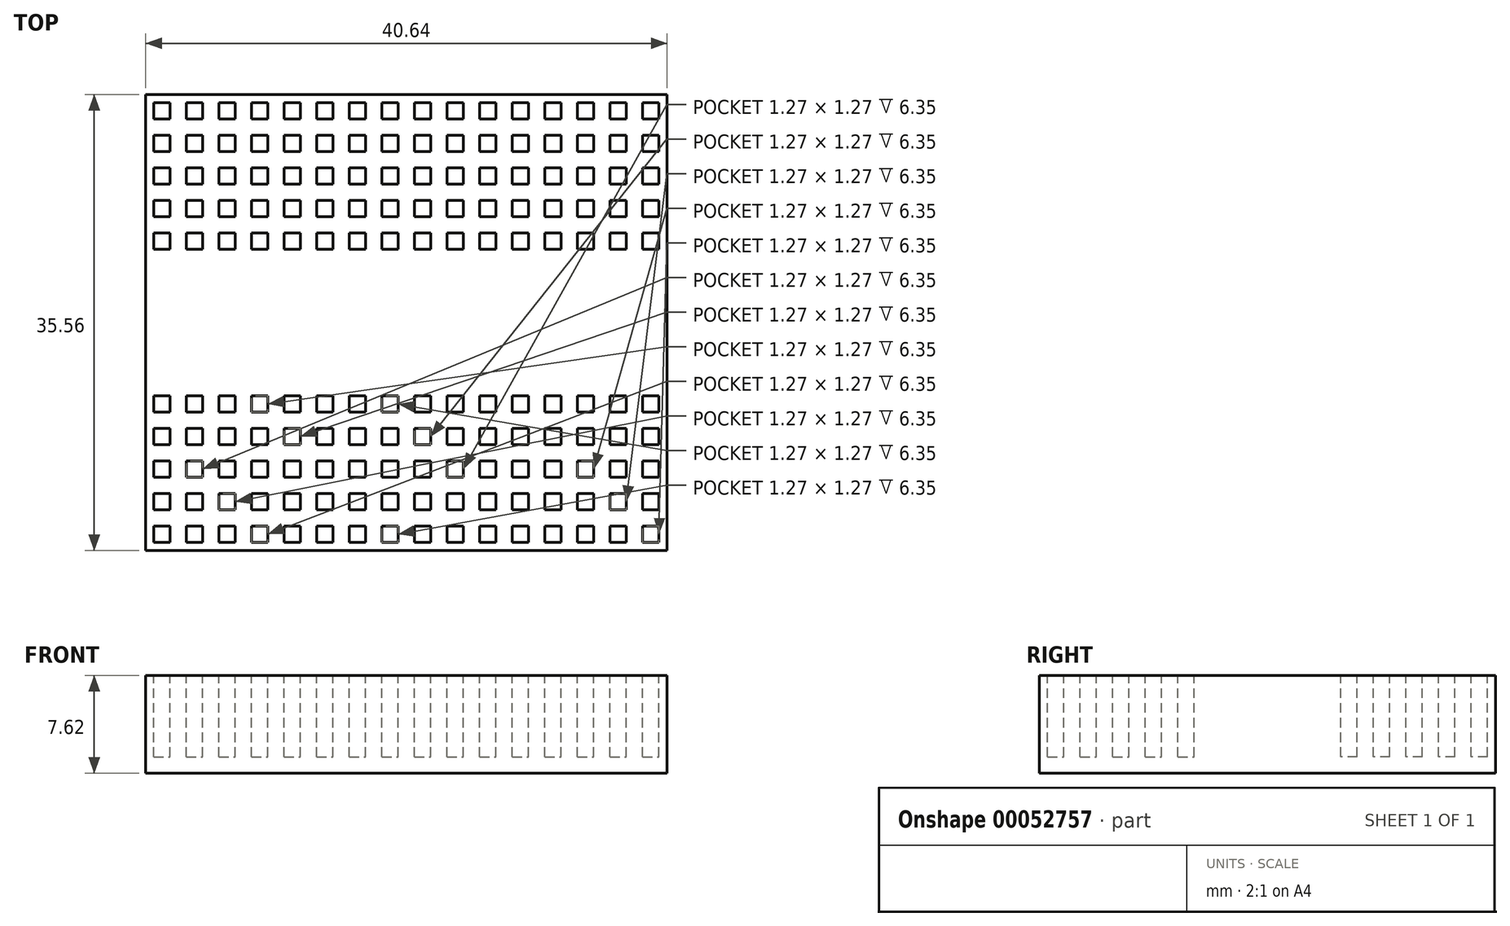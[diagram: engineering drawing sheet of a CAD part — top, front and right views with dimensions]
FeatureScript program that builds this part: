
annotation { "Feature Type Name" : "Feature", "Feature Type Description" : "" }
export const myFeature = defineFeature(function(context is Context, id is Id, definition is map)
    precondition{}
    {
        {
            var Q0;
            Q0=qCreatedBy(makeId("Top.planeOp"),FACE);
            var sketch = newSketch(context, id + "F0", { "sketchPlane" : qUnion([Q0])});
            skLineSegment(sketch, "E0.bottom", {"start": v(-20.32, 17.78) * mm, "end": v(20.32, 17.78) * mm});
            skLineSegment(sketch, "E0.top", {"start": v(-20.32, -17.78) * mm, "end": v(20.32, -17.78) * mm});
            skLineSegment(sketch, "E0.left", {"start": v(-20.32, 17.78) * mm, "end": v(-20.32, -17.78) * mm});
            skLineSegment(sketch, "E0.right", {"start": v(20.32, 17.78) * mm, "end": v(20.32, -17.78) * mm});
            skLineSegment(sketch, "E1", {"start": v(-20.32, 17.78) * mm, "end": v(20.32, -17.78) * mm, "construction": true});
            skSolve(sketch);
        }
        {
            var Q0;
            Q0 = qSketchRegion(id + "F0", true);
            extrude(context, id + "F1", {"entities" : qUnion([Q0]), "depth" : 7.62 * mm});
        }
        {
            var Q0;
            Q0=makeQuery(id+"F1.opExtrude","CAP_FACE",FACE,{"disambiguationData":[OSD([sQuery(id+"F0.wireOp",EDGE,"E0.bottom"),sQuery(id+"F0.wireOp",EDGE,"E0.top"),sQuery(id+"F0.wireOp",EDGE,"E0.left"),sQuery(id+"F0.wireOp",EDGE,"E0.right")])],"isStart":false});
            var sketch = newSketch(context, id + "F2", { "sketchPlane" : qUnion([Q0])});
            skLineSegment(sketch, "E2.bottom", {"start": v(-19.69, 17.15) * mm, "end": v(-18.42, 17.15) * mm});
            skLineSegment(sketch, "E2.top", {"start": v(-19.69, 15.88) * mm, "end": v(-18.42, 15.88) * mm});
            skLineSegment(sketch, "E2.left", {"start": v(-19.69, 17.15) * mm, "end": v(-19.69, 15.88) * mm});
            skLineSegment(sketch, "E2.right", {"start": v(-18.42, 17.15) * mm, "end": v(-18.42, 15.88) * mm});
            skLineSegment(sketch, "E3.0.1.0", {"start": v(-19.69, 14.6) * mm, "end": v(-18.42, 14.6) * mm});
            skLineSegment(sketch, "E3.0.1.1", {"start": v(-19.69, 14.6) * mm, "end": v(-19.69, 13.34) * mm});
            skLineSegment(sketch, "E3.0.1.2", {"start": v(-18.42, 14.6) * mm, "end": v(-18.42, 13.34) * mm});
            skLineSegment(sketch, "E3.0.1.3", {"start": v(-19.69, 13.34) * mm, "end": v(-18.42, 13.34) * mm});
            skLineSegment(sketch, "E3.0.2.0", {"start": v(-19.69, 12.07) * mm, "end": v(-18.42, 12.07) * mm});
            skLineSegment(sketch, "E3.0.2.1", {"start": v(-19.69, 12.07) * mm, "end": v(-19.69, 10.8) * mm});
            skLineSegment(sketch, "E3.0.2.2", {"start": v(-18.42, 12.07) * mm, "end": v(-18.42, 10.8) * mm});
            skLineSegment(sketch, "E3.0.2.3", {"start": v(-19.69, 10.8) * mm, "end": v(-18.42, 10.8) * mm});
            skLineSegment(sketch, "E3.0.3.0", {"start": v(-19.69, 9.53) * mm, "end": v(-18.42, 9.53) * mm});
            skLineSegment(sketch, "E3.0.3.1", {"start": v(-19.69, 9.53) * mm, "end": v(-19.69, 8.26) * mm});
            skLineSegment(sketch, "E3.0.3.2", {"start": v(-18.42, 9.53) * mm, "end": v(-18.42, 8.26) * mm});
            skLineSegment(sketch, "E3.0.3.3", {"start": v(-19.69, 8.26) * mm, "end": v(-18.42, 8.26) * mm});
            skLineSegment(sketch, "E3.0.4.0", {"start": v(-19.69, 6.99) * mm, "end": v(-18.42, 6.99) * mm});
            skLineSegment(sketch, "E3.0.4.1", {"start": v(-19.69, 6.99) * mm, "end": v(-19.69, 5.72) * mm});
            skLineSegment(sketch, "E3.0.4.2", {"start": v(-18.42, 6.99) * mm, "end": v(-18.42, 5.72) * mm});
            skLineSegment(sketch, "E3.0.4.3", {"start": v(-19.69, 5.72) * mm, "end": v(-18.42, 5.72) * mm});
            skLineSegment(sketch, "E3.1.0.0", {"start": v(-17.15, 17.15) * mm, "end": v(-15.88, 17.15) * mm});
            skLineSegment(sketch, "E3.1.0.1", {"start": v(-17.15, 17.15) * mm, "end": v(-17.15, 15.88) * mm});
            skLineSegment(sketch, "E3.1.0.2", {"start": v(-15.88, 17.15) * mm, "end": v(-15.88, 15.88) * mm});
            skLineSegment(sketch, "E3.1.0.3", {"start": v(-17.15, 15.88) * mm, "end": v(-15.88, 15.88) * mm});
            skLineSegment(sketch, "E3.1.1.0", {"start": v(-17.15, 14.6) * mm, "end": v(-15.88, 14.6) * mm});
            skLineSegment(sketch, "E3.1.1.1", {"start": v(-17.15, 14.6) * mm, "end": v(-17.15, 13.34) * mm});
            skLineSegment(sketch, "E3.1.1.2", {"start": v(-15.88, 14.6) * mm, "end": v(-15.88, 13.34) * mm});
            skLineSegment(sketch, "E3.1.1.3", {"start": v(-17.15, 13.34) * mm, "end": v(-15.88, 13.34) * mm});
            skLineSegment(sketch, "E3.1.2.0", {"start": v(-17.15, 12.07) * mm, "end": v(-15.88, 12.07) * mm});
            skLineSegment(sketch, "E3.1.2.1", {"start": v(-17.15, 12.07) * mm, "end": v(-17.15, 10.8) * mm});
            skLineSegment(sketch, "E3.1.2.2", {"start": v(-15.88, 12.07) * mm, "end": v(-15.88, 10.8) * mm});
            skLineSegment(sketch, "E3.1.2.3", {"start": v(-17.15, 10.8) * mm, "end": v(-15.88, 10.8) * mm});
            skLineSegment(sketch, "E3.1.3.0", {"start": v(-17.15, 9.53) * mm, "end": v(-15.88, 9.53) * mm});
            skLineSegment(sketch, "E3.1.3.1", {"start": v(-17.15, 9.53) * mm, "end": v(-17.15, 8.26) * mm});
            skLineSegment(sketch, "E3.1.3.2", {"start": v(-15.88, 9.53) * mm, "end": v(-15.88, 8.26) * mm});
            skLineSegment(sketch, "E3.1.3.3", {"start": v(-17.15, 8.26) * mm, "end": v(-15.88, 8.26) * mm});
            skLineSegment(sketch, "E3.1.4.0", {"start": v(-17.15, 6.99) * mm, "end": v(-15.88, 6.99) * mm});
            skLineSegment(sketch, "E3.1.4.1", {"start": v(-17.15, 6.99) * mm, "end": v(-17.15, 5.72) * mm});
            skLineSegment(sketch, "E3.1.4.2", {"start": v(-15.88, 6.99) * mm, "end": v(-15.88, 5.72) * mm});
            skLineSegment(sketch, "E3.1.4.3", {"start": v(-17.15, 5.72) * mm, "end": v(-15.88, 5.72) * mm});
            skLineSegment(sketch, "E3.2.0.0", {"start": v(-14.6, 17.15) * mm, "end": v(-13.34, 17.15) * mm});
            skLineSegment(sketch, "E3.2.0.1", {"start": v(-14.6, 17.15) * mm, "end": v(-14.6, 15.88) * mm});
            skLineSegment(sketch, "E3.2.0.2", {"start": v(-13.34, 17.15) * mm, "end": v(-13.34, 15.88) * mm});
            skLineSegment(sketch, "E3.2.0.3", {"start": v(-14.6, 15.88) * mm, "end": v(-13.34, 15.88) * mm});
            skLineSegment(sketch, "E3.2.1.0", {"start": v(-14.6, 14.6) * mm, "end": v(-13.34, 14.6) * mm});
            skLineSegment(sketch, "E3.2.1.1", {"start": v(-14.6, 14.6) * mm, "end": v(-14.6, 13.34) * mm});
            skLineSegment(sketch, "E3.2.1.2", {"start": v(-13.34, 14.6) * mm, "end": v(-13.34, 13.34) * mm});
            skLineSegment(sketch, "E3.2.1.3", {"start": v(-14.6, 13.34) * mm, "end": v(-13.34, 13.34) * mm});
            skLineSegment(sketch, "E3.2.2.0", {"start": v(-14.6, 12.07) * mm, "end": v(-13.34, 12.07) * mm});
            skLineSegment(sketch, "E3.2.2.1", {"start": v(-14.6, 12.07) * mm, "end": v(-14.6, 10.8) * mm});
            skLineSegment(sketch, "E3.2.2.2", {"start": v(-13.34, 12.07) * mm, "end": v(-13.34, 10.8) * mm});
            skLineSegment(sketch, "E3.2.2.3", {"start": v(-14.6, 10.8) * mm, "end": v(-13.34, 10.8) * mm});
            skLineSegment(sketch, "E3.2.3.0", {"start": v(-14.6, 9.53) * mm, "end": v(-13.34, 9.53) * mm});
            skLineSegment(sketch, "E3.2.3.1", {"start": v(-14.6, 9.53) * mm, "end": v(-14.6, 8.26) * mm});
            skLineSegment(sketch, "E3.2.3.2", {"start": v(-13.34, 9.53) * mm, "end": v(-13.34, 8.26) * mm});
            skLineSegment(sketch, "E3.2.3.3", {"start": v(-14.6, 8.26) * mm, "end": v(-13.34, 8.26) * mm});
            skLineSegment(sketch, "E3.2.4.0", {"start": v(-14.6, 6.99) * mm, "end": v(-13.34, 6.99) * mm});
            skLineSegment(sketch, "E3.2.4.1", {"start": v(-14.6, 6.99) * mm, "end": v(-14.6, 5.72) * mm});
            skLineSegment(sketch, "E3.2.4.2", {"start": v(-13.34, 6.99) * mm, "end": v(-13.34, 5.72) * mm});
            skLineSegment(sketch, "E3.2.4.3", {"start": v(-14.6, 5.72) * mm, "end": v(-13.34, 5.72) * mm});
            skLineSegment(sketch, "E3.3.0.0", {"start": v(-12.07, 17.15) * mm, "end": v(-10.8, 17.15) * mm});
            skLineSegment(sketch, "E3.3.0.1", {"start": v(-12.07, 17.15) * mm, "end": v(-12.07, 15.88) * mm});
            skLineSegment(sketch, "E3.3.0.2", {"start": v(-10.8, 17.15) * mm, "end": v(-10.8, 15.88) * mm});
            skLineSegment(sketch, "E3.3.0.3", {"start": v(-12.07, 15.88) * mm, "end": v(-10.8, 15.88) * mm});
            skLineSegment(sketch, "E3.3.1.0", {"start": v(-12.07, 14.6) * mm, "end": v(-10.8, 14.6) * mm});
            skLineSegment(sketch, "E3.3.1.1", {"start": v(-12.07, 14.6) * mm, "end": v(-12.07, 13.34) * mm});
            skLineSegment(sketch, "E3.3.1.2", {"start": v(-10.8, 14.6) * mm, "end": v(-10.8, 13.34) * mm});
            skLineSegment(sketch, "E3.3.1.3", {"start": v(-12.07, 13.34) * mm, "end": v(-10.8, 13.34) * mm});
            skLineSegment(sketch, "E3.3.2.0", {"start": v(-12.07, 12.07) * mm, "end": v(-10.8, 12.07) * mm});
            skLineSegment(sketch, "E3.3.2.1", {"start": v(-12.07, 12.07) * mm, "end": v(-12.07, 10.8) * mm});
            skLineSegment(sketch, "E3.3.2.2", {"start": v(-10.8, 12.07) * mm, "end": v(-10.8, 10.8) * mm});
            skLineSegment(sketch, "E3.3.2.3", {"start": v(-12.07, 10.8) * mm, "end": v(-10.8, 10.8) * mm});
            skLineSegment(sketch, "E3.3.3.0", {"start": v(-12.07, 9.53) * mm, "end": v(-10.8, 9.53) * mm});
            skLineSegment(sketch, "E3.3.3.1", {"start": v(-12.07, 9.53) * mm, "end": v(-12.07, 8.26) * mm});
            skLineSegment(sketch, "E3.3.3.2", {"start": v(-10.8, 9.53) * mm, "end": v(-10.8, 8.26) * mm});
            skLineSegment(sketch, "E3.3.3.3", {"start": v(-12.07, 8.26) * mm, "end": v(-10.8, 8.26) * mm});
            skLineSegment(sketch, "E3.3.4.0", {"start": v(-12.07, 6.99) * mm, "end": v(-10.8, 6.99) * mm});
            skLineSegment(sketch, "E3.3.4.1", {"start": v(-12.07, 6.99) * mm, "end": v(-12.07, 5.72) * mm});
            skLineSegment(sketch, "E3.3.4.2", {"start": v(-10.8, 6.99) * mm, "end": v(-10.8, 5.72) * mm});
            skLineSegment(sketch, "E3.3.4.3", {"start": v(-12.07, 5.72) * mm, "end": v(-10.8, 5.72) * mm});
            skLineSegment(sketch, "E3.4.0.0", {"start": v(-9.53, 17.15) * mm, "end": v(-8.26, 17.15) * mm});
            skLineSegment(sketch, "E3.4.0.1", {"start": v(-9.53, 17.15) * mm, "end": v(-9.53, 15.88) * mm});
            skLineSegment(sketch, "E3.4.0.2", {"start": v(-8.26, 17.15) * mm, "end": v(-8.26, 15.88) * mm});
            skLineSegment(sketch, "E3.4.0.3", {"start": v(-9.53, 15.88) * mm, "end": v(-8.26, 15.88) * mm});
            skLineSegment(sketch, "E3.4.1.0", {"start": v(-9.53, 14.6) * mm, "end": v(-8.26, 14.6) * mm});
            skLineSegment(sketch, "E3.4.1.1", {"start": v(-9.53, 14.6) * mm, "end": v(-9.53, 13.34) * mm});
            skLineSegment(sketch, "E3.4.1.2", {"start": v(-8.26, 14.6) * mm, "end": v(-8.26, 13.34) * mm});
            skLineSegment(sketch, "E3.4.1.3", {"start": v(-9.53, 13.34) * mm, "end": v(-8.26, 13.34) * mm});
            skLineSegment(sketch, "E3.4.2.0", {"start": v(-9.53, 12.07) * mm, "end": v(-8.26, 12.07) * mm});
            skLineSegment(sketch, "E3.4.2.1", {"start": v(-9.53, 12.07) * mm, "end": v(-9.53, 10.8) * mm});
            skLineSegment(sketch, "E3.4.2.2", {"start": v(-8.26, 12.07) * mm, "end": v(-8.26, 10.8) * mm});
            skLineSegment(sketch, "E3.4.2.3", {"start": v(-9.53, 10.8) * mm, "end": v(-8.26, 10.8) * mm});
            skLineSegment(sketch, "E3.4.3.0", {"start": v(-9.53, 9.53) * mm, "end": v(-8.26, 9.53) * mm});
            skLineSegment(sketch, "E3.4.3.1", {"start": v(-9.53, 9.53) * mm, "end": v(-9.53, 8.26) * mm});
            skLineSegment(sketch, "E3.4.3.2", {"start": v(-8.26, 9.53) * mm, "end": v(-8.26, 8.26) * mm});
            skLineSegment(sketch, "E3.4.3.3", {"start": v(-9.53, 8.26) * mm, "end": v(-8.26, 8.26) * mm});
            skLineSegment(sketch, "E3.4.4.0", {"start": v(-9.53, 6.99) * mm, "end": v(-8.26, 6.99) * mm});
            skLineSegment(sketch, "E3.4.4.1", {"start": v(-9.53, 6.99) * mm, "end": v(-9.53, 5.72) * mm});
            skLineSegment(sketch, "E3.4.4.2", {"start": v(-8.26, 6.99) * mm, "end": v(-8.26, 5.72) * mm});
            skLineSegment(sketch, "E3.4.4.3", {"start": v(-9.53, 5.72) * mm, "end": v(-8.26, 5.72) * mm});
            skLineSegment(sketch, "E3.5.0.0", {"start": v(-6.99, 17.15) * mm, "end": v(-5.72, 17.15) * mm});
            skLineSegment(sketch, "E3.5.0.1", {"start": v(-6.99, 17.15) * mm, "end": v(-6.99, 15.88) * mm});
            skLineSegment(sketch, "E3.5.0.2", {"start": v(-5.72, 17.15) * mm, "end": v(-5.72, 15.88) * mm});
            skLineSegment(sketch, "E3.5.0.3", {"start": v(-6.99, 15.88) * mm, "end": v(-5.72, 15.88) * mm});
            skLineSegment(sketch, "E3.5.1.0", {"start": v(-6.99, 14.6) * mm, "end": v(-5.72, 14.6) * mm});
            skLineSegment(sketch, "E3.5.1.1", {"start": v(-6.99, 14.6) * mm, "end": v(-6.99, 13.34) * mm});
            skLineSegment(sketch, "E3.5.1.2", {"start": v(-5.72, 14.6) * mm, "end": v(-5.72, 13.34) * mm});
            skLineSegment(sketch, "E3.5.1.3", {"start": v(-6.99, 13.34) * mm, "end": v(-5.72, 13.34) * mm});
            skLineSegment(sketch, "E3.5.2.0", {"start": v(-6.99, 12.07) * mm, "end": v(-5.72, 12.07) * mm});
            skLineSegment(sketch, "E3.5.2.1", {"start": v(-6.99, 12.07) * mm, "end": v(-6.99, 10.8) * mm});
            skLineSegment(sketch, "E3.5.2.2", {"start": v(-5.72, 12.07) * mm, "end": v(-5.72, 10.8) * mm});
            skLineSegment(sketch, "E3.5.2.3", {"start": v(-6.99, 10.8) * mm, "end": v(-5.72, 10.8) * mm});
            skLineSegment(sketch, "E3.5.3.0", {"start": v(-6.99, 9.53) * mm, "end": v(-5.72, 9.53) * mm});
            skLineSegment(sketch, "E3.5.3.1", {"start": v(-6.99, 9.53) * mm, "end": v(-6.99, 8.26) * mm});
            skLineSegment(sketch, "E3.5.3.2", {"start": v(-5.72, 9.53) * mm, "end": v(-5.72, 8.26) * mm});
            skLineSegment(sketch, "E3.5.3.3", {"start": v(-6.99, 8.26) * mm, "end": v(-5.72, 8.26) * mm});
            skLineSegment(sketch, "E3.5.4.0", {"start": v(-6.99, 6.99) * mm, "end": v(-5.72, 6.99) * mm});
            skLineSegment(sketch, "E3.5.4.1", {"start": v(-6.99, 6.99) * mm, "end": v(-6.99, 5.72) * mm});
            skLineSegment(sketch, "E3.5.4.2", {"start": v(-5.72, 6.99) * mm, "end": v(-5.72, 5.72) * mm});
            skLineSegment(sketch, "E3.5.4.3", {"start": v(-6.99, 5.72) * mm, "end": v(-5.72, 5.72) * mm});
            skLineSegment(sketch, "E3.6.0.0", {"start": v(-4.45, 17.15) * mm, "end": v(-3.18, 17.15) * mm});
            skLineSegment(sketch, "E3.6.0.1", {"start": v(-4.45, 17.15) * mm, "end": v(-4.45, 15.88) * mm});
            skLineSegment(sketch, "E3.6.0.2", {"start": v(-3.18, 17.15) * mm, "end": v(-3.18, 15.88) * mm});
            skLineSegment(sketch, "E3.6.0.3", {"start": v(-4.45, 15.88) * mm, "end": v(-3.18, 15.88) * mm});
            skLineSegment(sketch, "E3.6.1.0", {"start": v(-4.45, 14.6) * mm, "end": v(-3.18, 14.6) * mm});
            skLineSegment(sketch, "E3.6.1.1", {"start": v(-4.45, 14.6) * mm, "end": v(-4.45, 13.34) * mm});
            skLineSegment(sketch, "E3.6.1.2", {"start": v(-3.18, 14.6) * mm, "end": v(-3.18, 13.34) * mm});
            skLineSegment(sketch, "E3.6.1.3", {"start": v(-4.45, 13.34) * mm, "end": v(-3.18, 13.34) * mm});
            skLineSegment(sketch, "E3.6.2.0", {"start": v(-4.45, 12.07) * mm, "end": v(-3.18, 12.07) * mm});
            skLineSegment(sketch, "E3.6.2.1", {"start": v(-4.45, 12.07) * mm, "end": v(-4.45, 10.8) * mm});
            skLineSegment(sketch, "E3.6.2.2", {"start": v(-3.18, 12.07) * mm, "end": v(-3.18, 10.8) * mm});
            skLineSegment(sketch, "E3.6.2.3", {"start": v(-4.45, 10.8) * mm, "end": v(-3.18, 10.8) * mm});
            skLineSegment(sketch, "E3.6.3.0", {"start": v(-4.45, 9.53) * mm, "end": v(-3.18, 9.53) * mm});
            skLineSegment(sketch, "E3.6.3.1", {"start": v(-4.45, 9.53) * mm, "end": v(-4.45, 8.26) * mm});
            skLineSegment(sketch, "E3.6.3.2", {"start": v(-3.18, 9.53) * mm, "end": v(-3.18, 8.26) * mm});
            skLineSegment(sketch, "E3.6.3.3", {"start": v(-4.45, 8.26) * mm, "end": v(-3.18, 8.26) * mm});
            skLineSegment(sketch, "E3.6.4.0", {"start": v(-4.45, 6.99) * mm, "end": v(-3.18, 6.99) * mm});
            skLineSegment(sketch, "E3.6.4.1", {"start": v(-4.45, 6.99) * mm, "end": v(-4.45, 5.72) * mm});
            skLineSegment(sketch, "E3.6.4.2", {"start": v(-3.18, 6.99) * mm, "end": v(-3.18, 5.72) * mm});
            skLineSegment(sketch, "E3.6.4.3", {"start": v(-4.45, 5.72) * mm, "end": v(-3.18, 5.72) * mm});
            skLineSegment(sketch, "E3.7.0.0", {"start": v(-1.9, 17.15) * mm, "end": v(-0.64, 17.15) * mm});
            skLineSegment(sketch, "E3.7.0.1", {"start": v(-1.9, 17.15) * mm, "end": v(-1.9, 15.88) * mm});
            skLineSegment(sketch, "E3.7.0.2", {"start": v(-0.63, 17.15) * mm, "end": v(-0.64, 15.88) * mm});
            skLineSegment(sketch, "E3.7.0.3", {"start": v(-1.9, 15.88) * mm, "end": v(-0.64, 15.88) * mm});
            skLineSegment(sketch, "E3.7.1.0", {"start": v(-1.9, 14.6) * mm, "end": v(-0.64, 14.6) * mm});
            skLineSegment(sketch, "E3.7.1.1", {"start": v(-1.9, 14.6) * mm, "end": v(-1.9, 13.34) * mm});
            skLineSegment(sketch, "E3.7.1.2", {"start": v(-0.63, 14.6) * mm, "end": v(-0.64, 13.34) * mm});
            skLineSegment(sketch, "E3.7.1.3", {"start": v(-1.9, 13.34) * mm, "end": v(-0.64, 13.34) * mm});
            skLineSegment(sketch, "E3.7.2.0", {"start": v(-1.9, 12.07) * mm, "end": v(-0.64, 12.07) * mm});
            skLineSegment(sketch, "E3.7.2.1", {"start": v(-1.9, 12.07) * mm, "end": v(-1.9, 10.8) * mm});
            skLineSegment(sketch, "E3.7.2.2", {"start": v(-0.63, 12.07) * mm, "end": v(-0.64, 10.8) * mm});
            skLineSegment(sketch, "E3.7.2.3", {"start": v(-1.9, 10.8) * mm, "end": v(-0.64, 10.8) * mm});
            skLineSegment(sketch, "E3.7.3.0", {"start": v(-1.9, 9.53) * mm, "end": v(-0.64, 9.53) * mm});
            skLineSegment(sketch, "E3.7.3.1", {"start": v(-1.9, 9.53) * mm, "end": v(-1.9, 8.26) * mm});
            skLineSegment(sketch, "E3.7.3.2", {"start": v(-0.63, 9.53) * mm, "end": v(-0.64, 8.26) * mm});
            skLineSegment(sketch, "E3.7.3.3", {"start": v(-1.9, 8.26) * mm, "end": v(-0.64, 8.26) * mm});
            skLineSegment(sketch, "E3.7.4.0", {"start": v(-1.9, 6.99) * mm, "end": v(-0.64, 6.99) * mm});
            skLineSegment(sketch, "E3.7.4.1", {"start": v(-1.9, 6.99) * mm, "end": v(-1.9, 5.72) * mm});
            skLineSegment(sketch, "E3.7.4.2", {"start": v(-0.63, 6.99) * mm, "end": v(-0.64, 5.72) * mm});
            skLineSegment(sketch, "E3.7.4.3", {"start": v(-1.9, 5.72) * mm, "end": v(-0.64, 5.72) * mm});
            skLineSegment(sketch, "E3.8.0.0", {"start": v(0.64, 17.15) * mm, "end": v(1.9, 17.15) * mm});
            skLineSegment(sketch, "E3.8.0.1", {"start": v(0.64, 17.15) * mm, "end": v(0.64, 15.88) * mm});
            skLineSegment(sketch, "E3.8.0.2", {"start": v(1.9, 17.15) * mm, "end": v(1.9, 15.88) * mm});
            skLineSegment(sketch, "E3.8.0.3", {"start": v(0.64, 15.88) * mm, "end": v(1.9, 15.88) * mm});
            skLineSegment(sketch, "E3.8.1.0", {"start": v(0.64, 14.6) * mm, "end": v(1.9, 14.6) * mm});
            skLineSegment(sketch, "E3.8.1.1", {"start": v(0.64, 14.6) * mm, "end": v(0.64, 13.34) * mm});
            skLineSegment(sketch, "E3.8.1.2", {"start": v(1.9, 14.6) * mm, "end": v(1.9, 13.34) * mm});
            skLineSegment(sketch, "E3.8.1.3", {"start": v(0.64, 13.34) * mm, "end": v(1.9, 13.34) * mm});
            skLineSegment(sketch, "E3.8.2.0", {"start": v(0.64, 12.07) * mm, "end": v(1.9, 12.07) * mm});
            skLineSegment(sketch, "E3.8.2.1", {"start": v(0.64, 12.07) * mm, "end": v(0.64, 10.8) * mm});
            skLineSegment(sketch, "E3.8.2.2", {"start": v(1.9, 12.07) * mm, "end": v(1.9, 10.8) * mm});
            skLineSegment(sketch, "E3.8.2.3", {"start": v(0.64, 10.8) * mm, "end": v(1.9, 10.8) * mm});
            skLineSegment(sketch, "E3.8.3.0", {"start": v(0.64, 9.53) * mm, "end": v(1.9, 9.53) * mm});
            skLineSegment(sketch, "E3.8.3.1", {"start": v(0.64, 9.53) * mm, "end": v(0.64, 8.26) * mm});
            skLineSegment(sketch, "E3.8.3.2", {"start": v(1.9, 9.53) * mm, "end": v(1.9, 8.26) * mm});
            skLineSegment(sketch, "E3.8.3.3", {"start": v(0.64, 8.26) * mm, "end": v(1.9, 8.26) * mm});
            skLineSegment(sketch, "E3.8.4.0", {"start": v(0.64, 6.99) * mm, "end": v(1.9, 6.99) * mm});
            skLineSegment(sketch, "E3.8.4.1", {"start": v(0.64, 6.99) * mm, "end": v(0.64, 5.72) * mm});
            skLineSegment(sketch, "E3.8.4.2", {"start": v(1.9, 6.99) * mm, "end": v(1.9, 5.72) * mm});
            skLineSegment(sketch, "E3.8.4.3", {"start": v(0.64, 5.72) * mm, "end": v(1.9, 5.72) * mm});
            skLineSegment(sketch, "E3.9.0.0", {"start": v(3.18, 17.15) * mm, "end": v(4.45, 17.15) * mm});
            skLineSegment(sketch, "E3.9.0.1", {"start": v(3.18, 17.15) * mm, "end": v(3.18, 15.88) * mm});
            skLineSegment(sketch, "E3.9.0.2", {"start": v(4.45, 17.15) * mm, "end": v(4.45, 15.88) * mm});
            skLineSegment(sketch, "E3.9.0.3", {"start": v(3.18, 15.88) * mm, "end": v(4.45, 15.88) * mm});
            skLineSegment(sketch, "E3.9.1.0", {"start": v(3.18, 14.6) * mm, "end": v(4.45, 14.6) * mm});
            skLineSegment(sketch, "E3.9.1.1", {"start": v(3.18, 14.6) * mm, "end": v(3.18, 13.34) * mm});
            skLineSegment(sketch, "E3.9.1.2", {"start": v(4.45, 14.6) * mm, "end": v(4.45, 13.34) * mm});
            skLineSegment(sketch, "E3.9.1.3", {"start": v(3.18, 13.34) * mm, "end": v(4.45, 13.34) * mm});
            skLineSegment(sketch, "E3.9.2.0", {"start": v(3.18, 12.07) * mm, "end": v(4.45, 12.07) * mm});
            skLineSegment(sketch, "E3.9.2.1", {"start": v(3.18, 12.07) * mm, "end": v(3.18, 10.8) * mm});
            skLineSegment(sketch, "E3.9.2.2", {"start": v(4.45, 12.07) * mm, "end": v(4.45, 10.8) * mm});
            skLineSegment(sketch, "E3.9.2.3", {"start": v(3.18, 10.8) * mm, "end": v(4.45, 10.8) * mm});
            skLineSegment(sketch, "E3.9.3.0", {"start": v(3.18, 9.53) * mm, "end": v(4.45, 9.53) * mm});
            skLineSegment(sketch, "E3.9.3.1", {"start": v(3.18, 9.53) * mm, "end": v(3.18, 8.26) * mm});
            skLineSegment(sketch, "E3.9.3.2", {"start": v(4.45, 9.53) * mm, "end": v(4.45, 8.26) * mm});
            skLineSegment(sketch, "E3.9.3.3", {"start": v(3.18, 8.26) * mm, "end": v(4.45, 8.26) * mm});
            skLineSegment(sketch, "E3.9.4.0", {"start": v(3.18, 6.99) * mm, "end": v(4.45, 6.99) * mm});
            skLineSegment(sketch, "E3.9.4.1", {"start": v(3.18, 6.99) * mm, "end": v(3.18, 5.72) * mm});
            skLineSegment(sketch, "E3.9.4.2", {"start": v(4.45, 6.99) * mm, "end": v(4.45, 5.72) * mm});
            skLineSegment(sketch, "E3.9.4.3", {"start": v(3.18, 5.72) * mm, "end": v(4.45, 5.72) * mm});
            skLineSegment(sketch, "E3.10.0.0", {"start": v(5.72, 17.15) * mm, "end": v(6.99, 17.15) * mm});
            skLineSegment(sketch, "E3.10.0.1", {"start": v(5.72, 17.15) * mm, "end": v(5.72, 15.88) * mm});
            skLineSegment(sketch, "E3.10.0.2", {"start": v(6.99, 17.15) * mm, "end": v(6.99, 15.88) * mm});
            skLineSegment(sketch, "E3.10.0.3", {"start": v(5.72, 15.88) * mm, "end": v(6.99, 15.88) * mm});
            skLineSegment(sketch, "E3.10.1.0", {"start": v(5.72, 14.6) * mm, "end": v(6.99, 14.6) * mm});
            skLineSegment(sketch, "E3.10.1.1", {"start": v(5.72, 14.6) * mm, "end": v(5.72, 13.34) * mm});
            skLineSegment(sketch, "E3.10.1.2", {"start": v(6.99, 14.6) * mm, "end": v(6.99, 13.34) * mm});
            skLineSegment(sketch, "E3.10.1.3", {"start": v(5.72, 13.34) * mm, "end": v(6.99, 13.34) * mm});
            skLineSegment(sketch, "E3.10.2.0", {"start": v(5.72, 12.07) * mm, "end": v(6.99, 12.07) * mm});
            skLineSegment(sketch, "E3.10.2.1", {"start": v(5.72, 12.07) * mm, "end": v(5.72, 10.8) * mm});
            skLineSegment(sketch, "E3.10.2.2", {"start": v(6.99, 12.07) * mm, "end": v(6.99, 10.8) * mm});
            skLineSegment(sketch, "E3.10.2.3", {"start": v(5.72, 10.8) * mm, "end": v(6.99, 10.8) * mm});
            skLineSegment(sketch, "E3.10.3.0", {"start": v(5.72, 9.53) * mm, "end": v(6.99, 9.53) * mm});
            skLineSegment(sketch, "E3.10.3.1", {"start": v(5.72, 9.53) * mm, "end": v(5.72, 8.26) * mm});
            skLineSegment(sketch, "E3.10.3.2", {"start": v(6.99, 9.53) * mm, "end": v(6.99, 8.26) * mm});
            skLineSegment(sketch, "E3.10.3.3", {"start": v(5.72, 8.26) * mm, "end": v(6.99, 8.26) * mm});
            skLineSegment(sketch, "E3.10.4.0", {"start": v(5.72, 6.99) * mm, "end": v(6.99, 6.99) * mm});
            skLineSegment(sketch, "E3.10.4.1", {"start": v(5.72, 6.99) * mm, "end": v(5.72, 5.72) * mm});
            skLineSegment(sketch, "E3.10.4.2", {"start": v(6.99, 6.99) * mm, "end": v(6.99, 5.72) * mm});
            skLineSegment(sketch, "E3.10.4.3", {"start": v(5.72, 5.72) * mm, "end": v(6.99, 5.72) * mm});
            skLineSegment(sketch, "E3.11.0.0", {"start": v(8.26, 17.15) * mm, "end": v(9.53, 17.15) * mm});
            skLineSegment(sketch, "E3.11.0.1", {"start": v(8.26, 17.15) * mm, "end": v(8.26, 15.88) * mm});
            skLineSegment(sketch, "E3.11.0.2", {"start": v(9.53, 17.15) * mm, "end": v(9.53, 15.88) * mm});
            skLineSegment(sketch, "E3.11.0.3", {"start": v(8.26, 15.88) * mm, "end": v(9.53, 15.88) * mm});
            skLineSegment(sketch, "E3.11.1.0", {"start": v(8.26, 14.6) * mm, "end": v(9.53, 14.6) * mm});
            skLineSegment(sketch, "E3.11.1.1", {"start": v(8.26, 14.6) * mm, "end": v(8.26, 13.34) * mm});
            skLineSegment(sketch, "E3.11.1.2", {"start": v(9.53, 14.6) * mm, "end": v(9.53, 13.34) * mm});
            skLineSegment(sketch, "E3.11.1.3", {"start": v(8.26, 13.34) * mm, "end": v(9.53, 13.34) * mm});
            skLineSegment(sketch, "E3.11.2.0", {"start": v(8.26, 12.07) * mm, "end": v(9.53, 12.07) * mm});
            skLineSegment(sketch, "E3.11.2.1", {"start": v(8.26, 12.07) * mm, "end": v(8.26, 10.8) * mm});
            skLineSegment(sketch, "E3.11.2.2", {"start": v(9.53, 12.07) * mm, "end": v(9.53, 10.8) * mm});
            skLineSegment(sketch, "E3.11.2.3", {"start": v(8.26, 10.8) * mm, "end": v(9.53, 10.8) * mm});
            skLineSegment(sketch, "E3.11.3.0", {"start": v(8.26, 9.53) * mm, "end": v(9.53, 9.53) * mm});
            skLineSegment(sketch, "E3.11.3.1", {"start": v(8.26, 9.53) * mm, "end": v(8.26, 8.26) * mm});
            skLineSegment(sketch, "E3.11.3.2", {"start": v(9.53, 9.53) * mm, "end": v(9.53, 8.26) * mm});
            skLineSegment(sketch, "E3.11.3.3", {"start": v(8.26, 8.26) * mm, "end": v(9.53, 8.26) * mm});
            skLineSegment(sketch, "E3.11.4.0", {"start": v(8.26, 6.99) * mm, "end": v(9.53, 6.99) * mm});
            skLineSegment(sketch, "E3.11.4.1", {"start": v(8.26, 6.99) * mm, "end": v(8.26, 5.72) * mm});
            skLineSegment(sketch, "E3.11.4.2", {"start": v(9.53, 6.99) * mm, "end": v(9.53, 5.72) * mm});
            skLineSegment(sketch, "E3.11.4.3", {"start": v(8.26, 5.72) * mm, "end": v(9.53, 5.72) * mm});
            skLineSegment(sketch, "E3.12.0.0", {"start": v(10.8, 17.15) * mm, "end": v(12.07, 17.15) * mm});
            skLineSegment(sketch, "E3.12.0.1", {"start": v(10.8, 17.15) * mm, "end": v(10.8, 15.88) * mm});
            skLineSegment(sketch, "E3.12.0.2", {"start": v(12.07, 17.15) * mm, "end": v(12.07, 15.88) * mm});
            skLineSegment(sketch, "E3.12.0.3", {"start": v(10.8, 15.88) * mm, "end": v(12.07, 15.88) * mm});
            skLineSegment(sketch, "E3.12.1.0", {"start": v(10.8, 14.6) * mm, "end": v(12.07, 14.6) * mm});
            skLineSegment(sketch, "E3.12.1.1", {"start": v(10.8, 14.6) * mm, "end": v(10.8, 13.34) * mm});
            skLineSegment(sketch, "E3.12.1.2", {"start": v(12.07, 14.6) * mm, "end": v(12.07, 13.34) * mm});
            skLineSegment(sketch, "E3.12.1.3", {"start": v(10.8, 13.34) * mm, "end": v(12.07, 13.34) * mm});
            skLineSegment(sketch, "E3.12.2.0", {"start": v(10.8, 12.07) * mm, "end": v(12.07, 12.07) * mm});
            skLineSegment(sketch, "E3.12.2.1", {"start": v(10.8, 12.07) * mm, "end": v(10.8, 10.8) * mm});
            skLineSegment(sketch, "E3.12.2.2", {"start": v(12.07, 12.07) * mm, "end": v(12.07, 10.8) * mm});
            skLineSegment(sketch, "E3.12.2.3", {"start": v(10.8, 10.8) * mm, "end": v(12.07, 10.8) * mm});
            skLineSegment(sketch, "E3.12.3.0", {"start": v(10.8, 9.53) * mm, "end": v(12.07, 9.53) * mm});
            skLineSegment(sketch, "E3.12.3.1", {"start": v(10.8, 9.53) * mm, "end": v(10.8, 8.26) * mm});
            skLineSegment(sketch, "E3.12.3.2", {"start": v(12.07, 9.53) * mm, "end": v(12.07, 8.26) * mm});
            skLineSegment(sketch, "E3.12.3.3", {"start": v(10.8, 8.26) * mm, "end": v(12.07, 8.26) * mm});
            skLineSegment(sketch, "E3.12.4.0", {"start": v(10.8, 6.99) * mm, "end": v(12.07, 6.99) * mm});
            skLineSegment(sketch, "E3.12.4.1", {"start": v(10.8, 6.99) * mm, "end": v(10.8, 5.72) * mm});
            skLineSegment(sketch, "E3.12.4.2", {"start": v(12.07, 6.99) * mm, "end": v(12.07, 5.72) * mm});
            skLineSegment(sketch, "E3.12.4.3", {"start": v(10.8, 5.72) * mm, "end": v(12.07, 5.72) * mm});
            skLineSegment(sketch, "E3.13.0.0", {"start": v(13.34, 17.15) * mm, "end": v(14.6, 17.15) * mm});
            skLineSegment(sketch, "E3.13.0.1", {"start": v(13.34, 17.15) * mm, "end": v(13.34, 15.88) * mm});
            skLineSegment(sketch, "E3.13.0.2", {"start": v(14.6, 17.15) * mm, "end": v(14.6, 15.88) * mm});
            skLineSegment(sketch, "E3.13.0.3", {"start": v(13.34, 15.88) * mm, "end": v(14.6, 15.88) * mm});
            skLineSegment(sketch, "E3.13.1.0", {"start": v(13.34, 14.6) * mm, "end": v(14.6, 14.6) * mm});
            skLineSegment(sketch, "E3.13.1.1", {"start": v(13.34, 14.6) * mm, "end": v(13.34, 13.34) * mm});
            skLineSegment(sketch, "E3.13.1.2", {"start": v(14.6, 14.6) * mm, "end": v(14.6, 13.34) * mm});
            skLineSegment(sketch, "E3.13.1.3", {"start": v(13.34, 13.34) * mm, "end": v(14.6, 13.34) * mm});
            skLineSegment(sketch, "E3.13.2.0", {"start": v(13.34, 12.07) * mm, "end": v(14.6, 12.07) * mm});
            skLineSegment(sketch, "E3.13.2.1", {"start": v(13.34, 12.07) * mm, "end": v(13.34, 10.8) * mm});
            skLineSegment(sketch, "E3.13.2.2", {"start": v(14.6, 12.07) * mm, "end": v(14.6, 10.8) * mm});
            skLineSegment(sketch, "E3.13.2.3", {"start": v(13.34, 10.8) * mm, "end": v(14.6, 10.8) * mm});
            skLineSegment(sketch, "E3.13.3.0", {"start": v(13.34, 9.53) * mm, "end": v(14.6, 9.53) * mm});
            skLineSegment(sketch, "E3.13.3.1", {"start": v(13.34, 9.53) * mm, "end": v(13.34, 8.26) * mm});
            skLineSegment(sketch, "E3.13.3.2", {"start": v(14.6, 9.53) * mm, "end": v(14.6, 8.26) * mm});
            skLineSegment(sketch, "E3.13.3.3", {"start": v(13.34, 8.26) * mm, "end": v(14.6, 8.26) * mm});
            skLineSegment(sketch, "E3.13.4.0", {"start": v(13.34, 6.99) * mm, "end": v(14.6, 6.99) * mm});
            skLineSegment(sketch, "E3.13.4.1", {"start": v(13.34, 6.99) * mm, "end": v(13.34, 5.72) * mm});
            skLineSegment(sketch, "E3.13.4.2", {"start": v(14.6, 6.99) * mm, "end": v(14.6, 5.72) * mm});
            skLineSegment(sketch, "E3.13.4.3", {"start": v(13.34, 5.72) * mm, "end": v(14.6, 5.72) * mm});
            skLineSegment(sketch, "E3.14.0.0", {"start": v(15.88, 17.15) * mm, "end": v(17.15, 17.15) * mm});
            skLineSegment(sketch, "E3.14.0.1", {"start": v(15.88, 17.15) * mm, "end": v(15.88, 15.88) * mm});
            skLineSegment(sketch, "E3.14.0.2", {"start": v(17.15, 17.15) * mm, "end": v(17.15, 15.88) * mm});
            skLineSegment(sketch, "E3.14.0.3", {"start": v(15.88, 15.88) * mm, "end": v(17.15, 15.88) * mm});
            skLineSegment(sketch, "E3.14.1.0", {"start": v(15.88, 14.6) * mm, "end": v(17.15, 14.6) * mm});
            skLineSegment(sketch, "E3.14.1.1", {"start": v(15.88, 14.6) * mm, "end": v(15.88, 13.34) * mm});
            skLineSegment(sketch, "E3.14.1.2", {"start": v(17.15, 14.6) * mm, "end": v(17.15, 13.34) * mm});
            skLineSegment(sketch, "E3.14.1.3", {"start": v(15.88, 13.34) * mm, "end": v(17.15, 13.34) * mm});
            skLineSegment(sketch, "E3.14.2.0", {"start": v(15.88, 12.07) * mm, "end": v(17.15, 12.07) * mm});
            skLineSegment(sketch, "E3.14.2.1", {"start": v(15.88, 12.07) * mm, "end": v(15.88, 10.8) * mm});
            skLineSegment(sketch, "E3.14.2.2", {"start": v(17.15, 12.07) * mm, "end": v(17.15, 10.8) * mm});
            skLineSegment(sketch, "E3.14.2.3", {"start": v(15.88, 10.8) * mm, "end": v(17.15, 10.8) * mm});
            skLineSegment(sketch, "E3.14.3.0", {"start": v(15.88, 9.53) * mm, "end": v(17.15, 9.53) * mm});
            skLineSegment(sketch, "E3.14.3.1", {"start": v(15.88, 9.53) * mm, "end": v(15.88, 8.26) * mm});
            skLineSegment(sketch, "E3.14.3.2", {"start": v(17.15, 9.53) * mm, "end": v(17.15, 8.26) * mm});
            skLineSegment(sketch, "E3.14.3.3", {"start": v(15.88, 8.26) * mm, "end": v(17.15, 8.26) * mm});
            skLineSegment(sketch, "E3.14.4.0", {"start": v(15.88, 6.99) * mm, "end": v(17.15, 6.99) * mm});
            skLineSegment(sketch, "E3.14.4.1", {"start": v(15.88, 6.99) * mm, "end": v(15.88, 5.72) * mm});
            skLineSegment(sketch, "E3.14.4.2", {"start": v(17.15, 6.99) * mm, "end": v(17.15, 5.72) * mm});
            skLineSegment(sketch, "E3.14.4.3", {"start": v(15.88, 5.72) * mm, "end": v(17.15, 5.72) * mm});
            skLineSegment(sketch, "E3.15.0.0", {"start": v(18.42, 17.15) * mm, "end": v(19.69, 17.15) * mm});
            skLineSegment(sketch, "E3.15.0.1", {"start": v(18.42, 17.15) * mm, "end": v(18.42, 15.88) * mm});
            skLineSegment(sketch, "E3.15.0.2", {"start": v(19.69, 17.15) * mm, "end": v(19.69, 15.88) * mm});
            skLineSegment(sketch, "E3.15.0.3", {"start": v(18.42, 15.88) * mm, "end": v(19.69, 15.88) * mm});
            skLineSegment(sketch, "E3.15.1.0", {"start": v(18.42, 14.6) * mm, "end": v(19.69, 14.6) * mm});
            skLineSegment(sketch, "E3.15.1.1", {"start": v(18.42, 14.6) * mm, "end": v(18.42, 13.34) * mm});
            skLineSegment(sketch, "E3.15.1.2", {"start": v(19.69, 14.6) * mm, "end": v(19.69, 13.34) * mm});
            skLineSegment(sketch, "E3.15.1.3", {"start": v(18.42, 13.34) * mm, "end": v(19.69, 13.34) * mm});
            skLineSegment(sketch, "E3.15.2.0", {"start": v(18.42, 12.07) * mm, "end": v(19.69, 12.07) * mm});
            skLineSegment(sketch, "E3.15.2.1", {"start": v(18.42, 12.07) * mm, "end": v(18.42, 10.8) * mm});
            skLineSegment(sketch, "E3.15.2.2", {"start": v(19.69, 12.07) * mm, "end": v(19.69, 10.8) * mm});
            skLineSegment(sketch, "E3.15.2.3", {"start": v(18.42, 10.8) * mm, "end": v(19.69, 10.8) * mm});
            skLineSegment(sketch, "E3.15.3.0", {"start": v(18.42, 9.53) * mm, "end": v(19.69, 9.53) * mm});
            skLineSegment(sketch, "E3.15.3.1", {"start": v(18.42, 9.53) * mm, "end": v(18.42, 8.26) * mm});
            skLineSegment(sketch, "E3.15.3.2", {"start": v(19.69, 9.53) * mm, "end": v(19.69, 8.26) * mm});
            skLineSegment(sketch, "E3.15.3.3", {"start": v(18.42, 8.26) * mm, "end": v(19.69, 8.26) * mm});
            skLineSegment(sketch, "E3.15.4.0", {"start": v(18.42, 6.99) * mm, "end": v(19.69, 6.99) * mm});
            skLineSegment(sketch, "E3.15.4.1", {"start": v(18.42, 6.99) * mm, "end": v(18.42, 5.72) * mm});
            skLineSegment(sketch, "E3.15.4.2", {"start": v(19.69, 6.99) * mm, "end": v(19.69, 5.72) * mm});
            skLineSegment(sketch, "E3.15.4.3", {"start": v(18.42, 5.72) * mm, "end": v(19.69, 5.72) * mm});
            skLineSegment(sketch, "E3.direction1", {"start": v(-19.69, 17.15) * mm, "end": v(-17.15, 17.15) * mm, "construction": true});
            skLineSegment(sketch, "E3.direction2", {"start": v(-19.69, 17.15) * mm, "end": v(-19.69, 14.6) * mm, "construction": true});
            skLineSegment(sketch, "E4.MirrorCS", {"start": v(18.42, -6.99) * mm, "end": v(18.42, -5.72) * mm});
            skLineSegment(sketch, "E5.MirrorCS", {"start": v(18.42, -17.15) * mm, "end": v(18.42, -15.88) * mm});
            skLineSegment(sketch, "E6.MirrorCS", {"start": v(-17.15, -12.07) * mm, "end": v(-17.15, -10.8) * mm});
            skLineSegment(sketch, "E7.MirrorCS", {"start": v(-9.53, -9.53) * mm, "end": v(-9.53, -8.26) * mm});
            skLineSegment(sketch, "E8.MirrorCS", {"start": v(-12.07, -6.99) * mm, "end": v(-12.07, -5.72) * mm});
            skLineSegment(sketch, "E9.MirrorCS", {"start": v(-12.07, -17.15) * mm, "end": v(-12.07, -15.88) * mm});
            skLineSegment(sketch, "E10.MirrorCS", {"start": v(-14.6, -14.6) * mm, "end": v(-14.6, -13.34) * mm});
            skLineSegment(sketch, "E11.MirrorCS", {"start": v(-1.9, -6.99) * mm, "end": v(-1.9, -5.72) * mm});
            skLineSegment(sketch, "E12.MirrorCS", {"start": v(-1.9, -17.15) * mm, "end": v(-1.9, -15.88) * mm});
            skLineSegment(sketch, "E13.MirrorCS", {"start": v(-4.45, -14.6) * mm, "end": v(-4.45, -13.34) * mm});
            skLineSegment(sketch, "E14.MirrorCS", {"start": v(-6.99, -12.07) * mm, "end": v(-6.99, -10.8) * mm});
            skLineSegment(sketch, "E15.MirrorCS", {"start": v(8.26, -17.15) * mm, "end": v(8.26, -15.88) * mm});
            skLineSegment(sketch, "E16.MirrorCS", {"start": v(5.72, -14.6) * mm, "end": v(5.72, -13.34) * mm});
            skLineSegment(sketch, "E17.MirrorCS", {"start": v(3.18, -12.07) * mm, "end": v(3.18, -10.8) * mm});
            skLineSegment(sketch, "E18.MirrorCS", {"start": v(0.64, -9.53) * mm, "end": v(0.64, -8.26) * mm});
            skLineSegment(sketch, "E19.MirrorCS", {"start": v(15.88, -14.6) * mm, "end": v(15.88, -13.34) * mm});
            skLineSegment(sketch, "E20.MirrorCS", {"start": v(13.34, -12.07) * mm, "end": v(13.34, -10.8) * mm});
            skLineSegment(sketch, "E21.MirrorCS", {"start": v(10.8, -9.53) * mm, "end": v(10.8, -8.26) * mm});
            skLineSegment(sketch, "E22.MirrorCS", {"start": v(8.26, -6.99) * mm, "end": v(8.26, -5.72) * mm});
            skLineSegment(sketch, "E23.MirrorCS", {"start": v(-15.88, -12.07) * mm, "end": v(-15.88, -10.8) * mm});
            skLineSegment(sketch, "E24.MirrorCS", {"start": v(-8.26, -9.53) * mm, "end": v(-8.26, -8.26) * mm});
            skLineSegment(sketch, "E25.MirrorCS", {"start": v(-10.8, -6.99) * mm, "end": v(-10.8, -5.72) * mm});
            skLineSegment(sketch, "E26.MirrorCS", {"start": v(-10.8, -17.15) * mm, "end": v(-10.8, -15.88) * mm});
            skLineSegment(sketch, "E27.MirrorCS", {"start": v(-13.34, -14.6) * mm, "end": v(-13.34, -13.34) * mm});
            skLineSegment(sketch, "E28.MirrorCS", {"start": v(-0.63, -6.99) * mm, "end": v(-0.64, -5.72) * mm});
            skLineSegment(sketch, "E29.MirrorCS", {"start": v(-0.63, -17.15) * mm, "end": v(-0.64, -15.88) * mm});
            skLineSegment(sketch, "E30.MirrorCS", {"start": v(-3.18, -14.6) * mm, "end": v(-3.18, -13.34) * mm});
            skLineSegment(sketch, "E31.MirrorCS", {"start": v(-5.72, -12.07) * mm, "end": v(-5.72, -10.8) * mm});
            skLineSegment(sketch, "E32.MirrorCS", {"start": v(9.53, -17.15) * mm, "end": v(9.53, -15.88) * mm});
            skLineSegment(sketch, "E33.MirrorCS", {"start": v(6.99, -14.6) * mm, "end": v(6.99, -13.34) * mm});
            skLineSegment(sketch, "E34.MirrorCS", {"start": v(4.45, -12.07) * mm, "end": v(4.45, -10.8) * mm});
            skLineSegment(sketch, "E35.MirrorCS", {"start": v(1.9, -9.53) * mm, "end": v(1.9, -8.26) * mm});
            skLineSegment(sketch, "E36.MirrorCS", {"start": v(17.15, -14.6) * mm, "end": v(17.15, -13.34) * mm});
            skLineSegment(sketch, "E37.MirrorCS", {"start": v(14.6, -12.07) * mm, "end": v(14.6, -10.8) * mm});
            skLineSegment(sketch, "E38.MirrorCS", {"start": v(12.07, -9.53) * mm, "end": v(12.07, -8.26) * mm});
            skLineSegment(sketch, "E39.MirrorCS", {"start": v(9.53, -6.99) * mm, "end": v(9.53, -5.72) * mm});
            skLineSegment(sketch, "E40.MirrorCS", {"start": v(19.69, -6.99) * mm, "end": v(19.69, -5.72) * mm});
            skLineSegment(sketch, "E41.MirrorCS", {"start": v(19.69, -17.15) * mm, "end": v(19.69, -15.88) * mm});
            skLineSegment(sketch, "E42.MirrorCS", {"start": v(-17.15, -10.8) * mm, "end": v(-15.88, -10.8) * mm});
            skLineSegment(sketch, "E43.MirrorCS", {"start": v(-9.53, -8.26) * mm, "end": v(-8.26, -8.26) * mm});
            skLineSegment(sketch, "E44.MirrorCS", {"start": v(-12.07, -5.72) * mm, "end": v(-10.8, -5.72) * mm});
            skLineSegment(sketch, "E45.MirrorCS", {"start": v(-12.07, -15.88) * mm, "end": v(-10.8, -15.88) * mm});
            skLineSegment(sketch, "E46.MirrorCS", {"start": v(-14.6, -13.34) * mm, "end": v(-13.34, -13.34) * mm});
            skLineSegment(sketch, "E47.MirrorCS", {"start": v(-1.9, -5.72) * mm, "end": v(-0.64, -5.72) * mm});
            skLineSegment(sketch, "E48.MirrorCS", {"start": v(-1.9, -15.88) * mm, "end": v(-0.64, -15.88) * mm});
            skLineSegment(sketch, "E49.MirrorCS", {"start": v(-4.45, -13.34) * mm, "end": v(-3.18, -13.34) * mm});
            skLineSegment(sketch, "E50.MirrorCS", {"start": v(-6.99, -10.8) * mm, "end": v(-5.72, -10.8) * mm});
            skLineSegment(sketch, "E51.MirrorCS", {"start": v(8.26, -15.88) * mm, "end": v(9.53, -15.88) * mm});
            skLineSegment(sketch, "E52.MirrorCS", {"start": v(5.72, -13.34) * mm, "end": v(6.99, -13.34) * mm});
            skLineSegment(sketch, "E53.MirrorCS", {"start": v(3.18, -10.8) * mm, "end": v(4.45, -10.8) * mm});
            skLineSegment(sketch, "E54.MirrorCS", {"start": v(0.64, -8.26) * mm, "end": v(1.9, -8.26) * mm});
            skLineSegment(sketch, "E55.MirrorCS", {"start": v(15.88, -13.34) * mm, "end": v(17.15, -13.34) * mm});
            skLineSegment(sketch, "E56.MirrorCS", {"start": v(13.34, -10.8) * mm, "end": v(14.6, -10.8) * mm});
            skLineSegment(sketch, "E57.MirrorCS", {"start": v(10.8, -8.26) * mm, "end": v(12.07, -8.26) * mm});
            skLineSegment(sketch, "E58.MirrorCS", {"start": v(8.26, -5.72) * mm, "end": v(9.53, -5.72) * mm});
            skLineSegment(sketch, "E59.MirrorCS", {"start": v(18.42, -5.72) * mm, "end": v(19.69, -5.72) * mm});
            skLineSegment(sketch, "E60.MirrorCS", {"start": v(18.42, -15.88) * mm, "end": v(19.69, -15.88) * mm});
            skLineSegment(sketch, "E61.MirrorCS", {"start": v(-9.53, -6.99) * mm, "end": v(-8.26, -6.99) * mm});
            skLineSegment(sketch, "E62.MirrorCS", {"start": v(-9.53, -17.15) * mm, "end": v(-8.26, -17.15) * mm});
            skLineSegment(sketch, "E63.MirrorCS", {"start": v(-12.07, -14.6) * mm, "end": v(-10.8, -14.6) * mm});
            skLineSegment(sketch, "E64.MirrorCS", {"start": v(-14.6, -12.07) * mm, "end": v(-13.34, -12.07) * mm});
            skLineSegment(sketch, "E65.MirrorCS", {"start": v(0.64, -17.15) * mm, "end": v(1.9, -17.15) * mm});
            skLineSegment(sketch, "E66.MirrorCS", {"start": v(-1.9, -14.6) * mm, "end": v(-0.64, -14.6) * mm});
            skLineSegment(sketch, "E67.MirrorCS", {"start": v(-4.45, -12.07) * mm, "end": v(-3.18, -12.07) * mm});
            skLineSegment(sketch, "E68.MirrorCS", {"start": v(-6.99, -9.53) * mm, "end": v(-5.72, -9.53) * mm});
            skLineSegment(sketch, "E69.MirrorCS", {"start": v(8.26, -14.6) * mm, "end": v(9.53, -14.6) * mm});
            skLineSegment(sketch, "E70.MirrorCS", {"start": v(5.72, -12.07) * mm, "end": v(6.99, -12.07) * mm});
            skLineSegment(sketch, "E71.MirrorCS", {"start": v(3.18, -9.53) * mm, "end": v(4.45, -9.53) * mm});
            skLineSegment(sketch, "E72.MirrorCS", {"start": v(0.64, -6.99) * mm, "end": v(1.9, -6.99) * mm});
            skLineSegment(sketch, "E73.MirrorCS", {"start": v(15.88, -12.07) * mm, "end": v(17.15, -12.07) * mm});
            skLineSegment(sketch, "E74.MirrorCS", {"start": v(13.34, -9.53) * mm, "end": v(14.6, -9.53) * mm});
            skLineSegment(sketch, "E75.MirrorCS", {"start": v(10.8, -6.99) * mm, "end": v(12.07, -6.99) * mm});
            skLineSegment(sketch, "E76.MirrorCS", {"start": v(10.8, -17.15) * mm, "end": v(12.07, -17.15) * mm});
            skLineSegment(sketch, "E77.MirrorCS", {"start": v(18.42, -14.6) * mm, "end": v(19.69, -14.6) * mm});
            skLineSegment(sketch, "E78.MirrorCS", {"start": v(-17.15, -9.53) * mm, "end": v(-15.88, -9.53) * mm});
            skLineSegment(sketch, "E79.MirrorCS", {"start": v(-19.69, -6.99) * mm, "end": v(-18.42, -6.99) * mm});
            skLineSegment(sketch, "E80.MirrorCS", {"start": v(0.64, -17.15) * mm, "end": v(0.64, -15.88) * mm});
            skLineSegment(sketch, "E81.MirrorCS", {"start": v(-1.9, -14.6) * mm, "end": v(-1.9, -13.34) * mm});
            skLineSegment(sketch, "E82.MirrorCS", {"start": v(-4.45, -12.07) * mm, "end": v(-4.45, -10.8) * mm});
            skLineSegment(sketch, "E83.MirrorCS", {"start": v(-6.99, -9.53) * mm, "end": v(-6.99, -8.26) * mm});
            skLineSegment(sketch, "E84.MirrorCS", {"start": v(8.26, -14.6) * mm, "end": v(8.26, -13.34) * mm});
            skLineSegment(sketch, "E85.MirrorCS", {"start": v(5.72, -12.07) * mm, "end": v(5.72, -10.8) * mm});
            skLineSegment(sketch, "E86.MirrorCS", {"start": v(3.18, -9.53) * mm, "end": v(3.18, -8.26) * mm});
            skLineSegment(sketch, "E87.MirrorCS", {"start": v(0.64, -6.99) * mm, "end": v(0.64, -5.72) * mm});
            skLineSegment(sketch, "E88.MirrorCS", {"start": v(15.88, -12.07) * mm, "end": v(15.88, -10.8) * mm});
            skLineSegment(sketch, "E89.MirrorCS", {"start": v(13.34, -9.53) * mm, "end": v(13.34, -8.26) * mm});
            skLineSegment(sketch, "E90.MirrorCS", {"start": v(10.8, -6.99) * mm, "end": v(10.8, -5.72) * mm});
            skLineSegment(sketch, "E91.MirrorCS", {"start": v(10.8, -17.15) * mm, "end": v(10.8, -15.88) * mm});
            skLineSegment(sketch, "E92.MirrorCS", {"start": v(18.42, -14.6) * mm, "end": v(18.42, -13.34) * mm});
            skLineSegment(sketch, "E93.MirrorCS", {"start": v(-17.15, -9.53) * mm, "end": v(-17.15, -8.26) * mm});
            skLineSegment(sketch, "E94.MirrorCS", {"start": v(-19.69, -6.99) * mm, "end": v(-19.69, -5.72) * mm});
            skLineSegment(sketch, "E95.MirrorCS", {"start": v(-9.53, -6.99) * mm, "end": v(-9.53, -5.72) * mm});
            skLineSegment(sketch, "E96.MirrorCS", {"start": v(-9.53, -17.15) * mm, "end": v(-9.53, -15.88) * mm});
            skLineSegment(sketch, "E97.MirrorCS", {"start": v(-12.07, -14.6) * mm, "end": v(-12.07, -13.34) * mm});
            skLineSegment(sketch, "E98.MirrorCS", {"start": v(-14.6, -12.07) * mm, "end": v(-14.6, -10.8) * mm});
            skLineSegment(sketch, "E99.MirrorCS", {"start": v(9.53, -14.6) * mm, "end": v(9.53, -13.34) * mm});
            skLineSegment(sketch, "E100.MirrorCS", {"start": v(6.99, -12.07) * mm, "end": v(6.99, -10.8) * mm});
            skLineSegment(sketch, "E101.MirrorCS", {"start": v(4.45, -9.53) * mm, "end": v(4.45, -8.26) * mm});
            skLineSegment(sketch, "E102.MirrorCS", {"start": v(1.9, -6.99) * mm, "end": v(1.9, -5.72) * mm});
            skLineSegment(sketch, "E103.MirrorCS", {"start": v(17.15, -12.07) * mm, "end": v(17.15, -10.8) * mm});
            skLineSegment(sketch, "E104.MirrorCS", {"start": v(14.6, -9.53) * mm, "end": v(14.6, -8.26) * mm});
            skLineSegment(sketch, "E105.MirrorCS", {"start": v(12.07, -6.99) * mm, "end": v(12.07, -5.72) * mm});
            skLineSegment(sketch, "E106.MirrorCS", {"start": v(12.07, -17.15) * mm, "end": v(12.07, -15.88) * mm});
            skLineSegment(sketch, "E107.MirrorCS", {"start": v(19.69, -14.6) * mm, "end": v(19.69, -13.34) * mm});
            skLineSegment(sketch, "E108.MirrorCS", {"start": v(-15.88, -9.53) * mm, "end": v(-15.88, -8.26) * mm});
            skLineSegment(sketch, "E109.MirrorCS", {"start": v(-18.42, -6.99) * mm, "end": v(-18.42, -5.72) * mm});
            skLineSegment(sketch, "E110.MirrorCS", {"start": v(-8.26, -6.99) * mm, "end": v(-8.26, -5.72) * mm});
            skLineSegment(sketch, "E111.MirrorCS", {"start": v(-8.26, -17.15) * mm, "end": v(-8.26, -15.88) * mm});
            skLineSegment(sketch, "E112.MirrorCS", {"start": v(-10.8, -14.6) * mm, "end": v(-10.8, -13.34) * mm});
            skLineSegment(sketch, "E113.MirrorCS", {"start": v(-13.34, -12.07) * mm, "end": v(-13.34, -10.8) * mm});
            skLineSegment(sketch, "E114.MirrorCS", {"start": v(1.9, -17.15) * mm, "end": v(1.9, -15.88) * mm});
            skLineSegment(sketch, "E115.MirrorCS", {"start": v(-0.63, -14.6) * mm, "end": v(-0.64, -13.34) * mm});
            skLineSegment(sketch, "E116.MirrorCS", {"start": v(-3.18, -12.07) * mm, "end": v(-3.18, -10.8) * mm});
            skLineSegment(sketch, "E117.MirrorCS", {"start": v(-5.72, -9.53) * mm, "end": v(-5.72, -8.26) * mm});
            skLineSegment(sketch, "E118.MirrorCS", {"start": v(15.88, -10.8) * mm, "end": v(17.15, -10.8) * mm});
            skLineSegment(sketch, "E119.MirrorCS", {"start": v(13.34, -8.26) * mm, "end": v(14.6, -8.26) * mm});
            skLineSegment(sketch, "E120.MirrorCS", {"start": v(10.8, -5.72) * mm, "end": v(12.07, -5.72) * mm});
            skLineSegment(sketch, "E121.MirrorCS", {"start": v(10.8, -15.88) * mm, "end": v(12.07, -15.88) * mm});
            skLineSegment(sketch, "E122.MirrorCS", {"start": v(18.42, -13.34) * mm, "end": v(19.69, -13.34) * mm});
            skLineSegment(sketch, "E123.MirrorCS", {"start": v(-17.15, -8.26) * mm, "end": v(-15.88, -8.26) * mm});
            skLineSegment(sketch, "E124.MirrorCS", {"start": v(-19.69, -5.72) * mm, "end": v(-18.42, -5.72) * mm});
            skLineSegment(sketch, "E125.MirrorCS", {"start": v(-9.53, -5.72) * mm, "end": v(-8.26, -5.72) * mm});
            skLineSegment(sketch, "E126.MirrorCS", {"start": v(-9.53, -15.88) * mm, "end": v(-8.26, -15.88) * mm});
            skLineSegment(sketch, "E127.MirrorCS", {"start": v(-12.07, -13.34) * mm, "end": v(-10.8, -13.34) * mm});
            skLineSegment(sketch, "E128.MirrorCS", {"start": v(-14.6, -10.8) * mm, "end": v(-13.34, -10.8) * mm});
            skLineSegment(sketch, "E129.MirrorCS", {"start": v(0.64, -15.88) * mm, "end": v(1.9, -15.88) * mm});
            skLineSegment(sketch, "E130.MirrorCS", {"start": v(-1.9, -13.34) * mm, "end": v(-0.64, -13.34) * mm});
            skLineSegment(sketch, "E131.MirrorCS", {"start": v(-4.45, -10.8) * mm, "end": v(-3.18, -10.8) * mm});
            skLineSegment(sketch, "E132.MirrorCS", {"start": v(-6.99, -8.26) * mm, "end": v(-5.72, -8.26) * mm});
            skLineSegment(sketch, "E133.MirrorCS", {"start": v(8.26, -13.34) * mm, "end": v(9.53, -13.34) * mm});
            skLineSegment(sketch, "E134.MirrorCS", {"start": v(5.72, -10.8) * mm, "end": v(6.99, -10.8) * mm});
            skLineSegment(sketch, "E135.MirrorCS", {"start": v(3.18, -8.26) * mm, "end": v(4.45, -8.26) * mm});
            skLineSegment(sketch, "E136.MirrorCS", {"start": v(0.64, -5.72) * mm, "end": v(1.9, -5.72) * mm});
            skLineSegment(sketch, "E137.MirrorCS", {"start": v(18.42, -12.07) * mm, "end": v(19.69, -12.07) * mm});
            skLineSegment(sketch, "E138.MirrorCS", {"start": v(-17.15, -6.99) * mm, "end": v(-15.88, -6.99) * mm});
            skLineSegment(sketch, "E139.MirrorCS", {"start": v(-17.15, -17.15) * mm, "end": v(-15.88, -17.15) * mm});
            skLineSegment(sketch, "E140.MirrorCS", {"start": v(-6.99, -17.15) * mm, "end": v(-5.72, -17.15) * mm});
            skLineSegment(sketch, "E141.MirrorCS", {"start": v(-9.53, -14.6) * mm, "end": v(-8.26, -14.6) * mm});
            skLineSegment(sketch, "E142.MirrorCS", {"start": v(-12.07, -12.07) * mm, "end": v(-10.8, -12.07) * mm});
            skLineSegment(sketch, "E143.MirrorCS", {"start": v(-14.6, -9.53) * mm, "end": v(-13.34, -9.53) * mm});
            skLineSegment(sketch, "E144.MirrorCS", {"start": v(0.64, -14.6) * mm, "end": v(1.9, -14.6) * mm});
            skLineSegment(sketch, "E145.MirrorCS", {"start": v(-1.9, -12.07) * mm, "end": v(-0.64, -12.07) * mm});
            skLineSegment(sketch, "E146.MirrorCS", {"start": v(-4.45, -9.53) * mm, "end": v(-3.18, -9.53) * mm});
            skLineSegment(sketch, "E147.MirrorCS", {"start": v(-6.99, -6.99) * mm, "end": v(-5.72, -6.99) * mm});
            skLineSegment(sketch, "E148.MirrorCS", {"start": v(8.26, -12.07) * mm, "end": v(9.53, -12.07) * mm});
            skLineSegment(sketch, "E149.MirrorCS", {"start": v(5.72, -9.53) * mm, "end": v(6.99, -9.53) * mm});
            skLineSegment(sketch, "E150.MirrorCS", {"start": v(3.18, -6.99) * mm, "end": v(4.45, -6.99) * mm});
            skLineSegment(sketch, "E151.MirrorCS", {"start": v(3.18, -17.15) * mm, "end": v(4.45, -17.15) * mm});
            skLineSegment(sketch, "E152.MirrorCS", {"start": v(15.88, -9.53) * mm, "end": v(17.15, -9.53) * mm});
            skLineSegment(sketch, "E153.MirrorCS", {"start": v(13.34, -6.99) * mm, "end": v(14.6, -6.99) * mm});
            skLineSegment(sketch, "E154.MirrorCS", {"start": v(13.34, -17.15) * mm, "end": v(14.6, -17.15) * mm});
            skLineSegment(sketch, "E155.MirrorCS", {"start": v(10.8, -14.6) * mm, "end": v(12.07, -14.6) * mm});
            skLineSegment(sketch, "E156.MirrorCS", {"start": v(-17.15, -6.99) * mm, "end": v(-17.15, -5.72) * mm});
            skLineSegment(sketch, "E157.MirrorCS", {"start": v(-17.15, -17.15) * mm, "end": v(-17.15, -15.88) * mm});
            skLineSegment(sketch, "E158.MirrorCS", {"start": v(-6.99, -17.15) * mm, "end": v(-6.99, -15.88) * mm});
            skLineSegment(sketch, "E159.MirrorCS", {"start": v(-9.53, -14.6) * mm, "end": v(-9.53, -13.34) * mm});
            skLineSegment(sketch, "E160.MirrorCS", {"start": v(-12.07, -12.07) * mm, "end": v(-12.07, -10.8) * mm});
            skLineSegment(sketch, "E161.MirrorCS", {"start": v(-14.6, -9.53) * mm, "end": v(-14.6, -8.26) * mm});
            skLineSegment(sketch, "E162.MirrorCS", {"start": v(0.64, -14.6) * mm, "end": v(0.64, -13.34) * mm});
            skLineSegment(sketch, "E163.MirrorCS", {"start": v(-1.9, -12.07) * mm, "end": v(-1.9, -10.8) * mm});
            skLineSegment(sketch, "E164.MirrorCS", {"start": v(-4.45, -9.53) * mm, "end": v(-4.45, -8.26) * mm});
            skLineSegment(sketch, "E165.MirrorCS", {"start": v(-6.99, -6.99) * mm, "end": v(-6.99, -5.72) * mm});
            skLineSegment(sketch, "E166.MirrorCS", {"start": v(8.26, -12.07) * mm, "end": v(8.26, -10.8) * mm});
            skLineSegment(sketch, "E167.MirrorCS", {"start": v(5.72, -9.53) * mm, "end": v(5.72, -8.26) * mm});
            skLineSegment(sketch, "E168.MirrorCS", {"start": v(3.18, -6.99) * mm, "end": v(3.18, -5.72) * mm});
            skLineSegment(sketch, "E169.MirrorCS", {"start": v(3.18, -17.15) * mm, "end": v(3.18, -15.88) * mm});
            skLineSegment(sketch, "E170.MirrorCS", {"start": v(15.88, -9.53) * mm, "end": v(15.88, -8.26) * mm});
            skLineSegment(sketch, "E171.MirrorCS", {"start": v(13.34, -6.99) * mm, "end": v(13.34, -5.72) * mm});
            skLineSegment(sketch, "E172.MirrorCS", {"start": v(13.34, -17.15) * mm, "end": v(13.34, -15.88) * mm});
            skLineSegment(sketch, "E173.MirrorCS", {"start": v(10.8, -14.6) * mm, "end": v(10.8, -13.34) * mm});
            skLineSegment(sketch, "E174.MirrorCS", {"start": v(18.42, -12.07) * mm, "end": v(18.42, -10.8) * mm});
            skLineSegment(sketch, "E175.MirrorCS", {"start": v(-15.88, -6.99) * mm, "end": v(-15.88, -5.72) * mm});
            skLineSegment(sketch, "E176.MirrorCS", {"start": v(-15.88, -17.15) * mm, "end": v(-15.88, -15.88) * mm});
            skLineSegment(sketch, "E177.MirrorCS", {"start": v(-8.26, -14.6) * mm, "end": v(-8.26, -13.34) * mm});
            skLineSegment(sketch, "E178.MirrorCS", {"start": v(-5.72, -17.15) * mm, "end": v(-5.72, -15.88) * mm});
            skLineSegment(sketch, "E179.MirrorCS", {"start": v(-10.8, -12.07) * mm, "end": v(-10.8, -10.8) * mm});
            skLineSegment(sketch, "E180.MirrorCS", {"start": v(-13.34, -9.53) * mm, "end": v(-13.34, -8.26) * mm});
            skLineSegment(sketch, "E181.MirrorCS", {"start": v(1.9, -14.6) * mm, "end": v(1.9, -13.34) * mm});
            skLineSegment(sketch, "E182.MirrorCS", {"start": v(-0.63, -12.07) * mm, "end": v(-0.64, -10.8) * mm});
            skLineSegment(sketch, "E183.MirrorCS", {"start": v(-3.18, -9.53) * mm, "end": v(-3.18, -8.26) * mm});
            skLineSegment(sketch, "E184.MirrorCS", {"start": v(-5.72, -6.99) * mm, "end": v(-5.72, -5.72) * mm});
            skLineSegment(sketch, "E185.MirrorCS", {"start": v(9.53, -12.07) * mm, "end": v(9.53, -10.8) * mm});
            skLineSegment(sketch, "E186.MirrorCS", {"start": v(6.99, -9.53) * mm, "end": v(6.99, -8.26) * mm});
            skLineSegment(sketch, "E187.MirrorCS", {"start": v(4.45, -6.99) * mm, "end": v(4.45, -5.72) * mm});
            skLineSegment(sketch, "E188.MirrorCS", {"start": v(17.15, -9.53) * mm, "end": v(17.15, -8.26) * mm});
            skLineSegment(sketch, "E189.MirrorCS", {"start": v(4.45, -17.15) * mm, "end": v(4.45, -15.88) * mm});
            skLineSegment(sketch, "E190.MirrorCS", {"start": v(14.6, -6.99) * mm, "end": v(14.6, -5.72) * mm});
            skLineSegment(sketch, "E191.MirrorCS", {"start": v(14.6, -17.15) * mm, "end": v(14.6, -15.88) * mm});
            skLineSegment(sketch, "E192.MirrorCS", {"start": v(19.69, -12.07) * mm, "end": v(19.69, -10.8) * mm});
            skLineSegment(sketch, "E193.MirrorCS", {"start": v(12.07, -14.6) * mm, "end": v(12.07, -13.34) * mm});
            skLineSegment(sketch, "E194.MirrorCS", {"start": v(-12.07, -10.8) * mm, "end": v(-10.8, -10.8) * mm});
            skLineSegment(sketch, "E195.MirrorCS", {"start": v(-14.6, -8.26) * mm, "end": v(-13.34, -8.26) * mm});
            skLineSegment(sketch, "E196.MirrorCS", {"start": v(-17.15, -5.72) * mm, "end": v(-15.88, -5.72) * mm});
            skLineSegment(sketch, "E197.MirrorCS", {"start": v(-17.15, -15.88) * mm, "end": v(-15.88, -15.88) * mm});
            skLineSegment(sketch, "E198.MirrorCS", {"start": v(-4.45, -8.26) * mm, "end": v(-3.18, -8.26) * mm});
            skLineSegment(sketch, "E199.MirrorCS", {"start": v(-6.99, -5.72) * mm, "end": v(-5.72, -5.72) * mm});
            skLineSegment(sketch, "E200.MirrorCS", {"start": v(-6.99, -15.88) * mm, "end": v(-5.72, -15.88) * mm});
            skLineSegment(sketch, "E201.MirrorCS", {"start": v(-9.53, -13.34) * mm, "end": v(-8.26, -13.34) * mm});
            skLineSegment(sketch, "E202.MirrorCS", {"start": v(3.18, -5.72) * mm, "end": v(4.45, -5.72) * mm});
            skLineSegment(sketch, "E203.MirrorCS", {"start": v(3.18, -15.88) * mm, "end": v(4.45, -15.88) * mm});
            skLineSegment(sketch, "E204.MirrorCS", {"start": v(0.64, -13.34) * mm, "end": v(1.9, -13.34) * mm});
            skLineSegment(sketch, "E205.MirrorCS", {"start": v(-1.9, -10.8) * mm, "end": v(-0.64, -10.8) * mm});
            skLineSegment(sketch, "E206.MirrorCS", {"start": v(13.34, -15.88) * mm, "end": v(14.6, -15.88) * mm});
            skLineSegment(sketch, "E207.MirrorCS", {"start": v(10.8, -13.34) * mm, "end": v(12.07, -13.34) * mm});
            skLineSegment(sketch, "E208.MirrorCS", {"start": v(8.26, -10.8) * mm, "end": v(9.53, -10.8) * mm});
            skLineSegment(sketch, "E209.MirrorCS", {"start": v(5.72, -8.26) * mm, "end": v(6.99, -8.26) * mm});
            skLineSegment(sketch, "E210.MirrorCS", {"start": v(18.42, -10.8) * mm, "end": v(19.69, -10.8) * mm});
            skLineSegment(sketch, "E211.MirrorCS", {"start": v(15.88, -8.26) * mm, "end": v(17.15, -8.26) * mm});
            skLineSegment(sketch, "E212.MirrorCS", {"start": v(13.34, -5.72) * mm, "end": v(14.6, -5.72) * mm});
            skLineSegment(sketch, "E213.MirrorCS", {"start": v(-12.07, -9.53) * mm, "end": v(-10.8, -9.53) * mm});
            skLineSegment(sketch, "E214.MirrorCS", {"start": v(-14.6, -6.99) * mm, "end": v(-13.34, -6.99) * mm});
            skLineSegment(sketch, "E215.MirrorCS", {"start": v(-14.6, -17.15) * mm, "end": v(-13.34, -17.15) * mm});
            skLineSegment(sketch, "E216.MirrorCS", {"start": v(-17.15, -14.6) * mm, "end": v(-15.88, -14.6) * mm});
            skLineSegment(sketch, "E217.MirrorCS", {"start": v(-4.45, -6.99) * mm, "end": v(-3.18, -6.99) * mm});
            skLineSegment(sketch, "E218.MirrorCS", {"start": v(-4.45, -17.15) * mm, "end": v(-3.18, -17.15) * mm});
            skLineSegment(sketch, "E219.MirrorCS", {"start": v(-6.99, -14.6) * mm, "end": v(-5.72, -14.6) * mm});
            skLineSegment(sketch, "E220.MirrorCS", {"start": v(-9.53, -12.07) * mm, "end": v(-8.26, -12.07) * mm});
            skLineSegment(sketch, "E221.MirrorCS", {"start": v(5.72, -17.15) * mm, "end": v(6.99, -17.15) * mm});
            skLineSegment(sketch, "E222.MirrorCS", {"start": v(3.18, -14.6) * mm, "end": v(4.45, -14.6) * mm});
            skLineSegment(sketch, "E223.MirrorCS", {"start": v(0.64, -12.07) * mm, "end": v(1.9, -12.07) * mm});
            skLineSegment(sketch, "E224.MirrorCS", {"start": v(-1.9, -9.53) * mm, "end": v(-0.64, -9.53) * mm});
            skLineSegment(sketch, "E225.MirrorCS", {"start": v(13.34, -14.6) * mm, "end": v(14.6, -14.6) * mm});
            skLineSegment(sketch, "E226.MirrorCS", {"start": v(10.8, -12.07) * mm, "end": v(12.07, -12.07) * mm});
            skLineSegment(sketch, "E227.MirrorCS", {"start": v(8.26, -9.53) * mm, "end": v(9.53, -9.53) * mm});
            skLineSegment(sketch, "E228.MirrorCS", {"start": v(5.72, -6.99) * mm, "end": v(6.99, -6.99) * mm});
            skLineSegment(sketch, "E229.MirrorCS", {"start": v(18.42, -9.53) * mm, "end": v(19.69, -9.53) * mm});
            skLineSegment(sketch, "E230.MirrorCS", {"start": v(15.88, -6.99) * mm, "end": v(17.15, -6.99) * mm});
            skLineSegment(sketch, "E231.MirrorCS", {"start": v(15.88, -17.15) * mm, "end": v(17.15, -17.15) * mm});
            skLineSegment(sketch, "E232.MirrorCS", {"start": v(-12.07, -9.53) * mm, "end": v(-12.07, -8.26) * mm});
            skLineSegment(sketch, "E233.MirrorCS", {"start": v(-14.6, -6.99) * mm, "end": v(-14.6, -5.72) * mm});
            skLineSegment(sketch, "E234.MirrorCS", {"start": v(-14.6, -17.15) * mm, "end": v(-14.6, -15.88) * mm});
            skLineSegment(sketch, "E235.MirrorCS", {"start": v(-17.15, -14.6) * mm, "end": v(-17.15, -13.34) * mm});
            skLineSegment(sketch, "E236.MirrorCS", {"start": v(-4.45, -6.99) * mm, "end": v(-4.45, -5.72) * mm});
            skLineSegment(sketch, "E237.MirrorCS", {"start": v(-4.45, -17.15) * mm, "end": v(-4.45, -15.88) * mm});
            skLineSegment(sketch, "E238.MirrorCS", {"start": v(-6.99, -14.6) * mm, "end": v(-6.99, -13.34) * mm});
            skLineSegment(sketch, "E239.MirrorCS", {"start": v(-9.53, -12.07) * mm, "end": v(-9.53, -10.8) * mm});
            skLineSegment(sketch, "E240.MirrorCS", {"start": v(5.72, -17.15) * mm, "end": v(5.72, -15.88) * mm});
            skLineSegment(sketch, "E241.MirrorCS", {"start": v(3.18, -14.6) * mm, "end": v(3.18, -13.34) * mm});
            skLineSegment(sketch, "E242.MirrorCS", {"start": v(0.64, -12.07) * mm, "end": v(0.64, -10.8) * mm});
            skLineSegment(sketch, "E243.MirrorCS", {"start": v(-1.9, -9.53) * mm, "end": v(-1.9, -8.26) * mm});
            skLineSegment(sketch, "E244.MirrorCS", {"start": v(13.34, -14.6) * mm, "end": v(13.34, -13.34) * mm});
            skLineSegment(sketch, "E245.MirrorCS", {"start": v(10.8, -12.07) * mm, "end": v(10.8, -10.8) * mm});
            skLineSegment(sketch, "E246.MirrorCS", {"start": v(8.26, -9.53) * mm, "end": v(8.26, -8.26) * mm});
            skLineSegment(sketch, "E247.MirrorCS", {"start": v(5.72, -6.99) * mm, "end": v(5.72, -5.72) * mm});
            skLineSegment(sketch, "E248.MirrorCS", {"start": v(18.42, -9.53) * mm, "end": v(18.42, -8.26) * mm});
            skLineSegment(sketch, "E249.MirrorCS", {"start": v(15.88, -6.99) * mm, "end": v(15.88, -5.72) * mm});
            skLineSegment(sketch, "E250.MirrorCS", {"start": v(15.88, -17.15) * mm, "end": v(15.88, -15.88) * mm});
            skLineSegment(sketch, "E251.MirrorCS", {"start": v(-10.8, -9.53) * mm, "end": v(-10.8, -8.26) * mm});
            skLineSegment(sketch, "E252.MirrorCS", {"start": v(-13.34, -6.99) * mm, "end": v(-13.34, -5.72) * mm});
            skLineSegment(sketch, "E253.MirrorCS", {"start": v(-13.34, -17.15) * mm, "end": v(-13.34, -15.88) * mm});
            skLineSegment(sketch, "E254.MirrorCS", {"start": v(-15.88, -14.6) * mm, "end": v(-15.88, -13.34) * mm});
            skLineSegment(sketch, "E255.MirrorCS", {"start": v(-3.18, -6.99) * mm, "end": v(-3.18, -5.72) * mm});
            skLineSegment(sketch, "E256.MirrorCS", {"start": v(-3.18, -17.15) * mm, "end": v(-3.18, -15.88) * mm});
            skLineSegment(sketch, "E257.MirrorCS", {"start": v(-5.72, -14.6) * mm, "end": v(-5.72, -13.34) * mm});
            skLineSegment(sketch, "E258.MirrorCS", {"start": v(-8.26, -12.07) * mm, "end": v(-8.26, -10.8) * mm});
            skLineSegment(sketch, "E259.MirrorCS", {"start": v(6.99, -17.15) * mm, "end": v(6.99, -15.88) * mm});
            skLineSegment(sketch, "E260.MirrorCS", {"start": v(4.45, -14.6) * mm, "end": v(4.45, -13.34) * mm});
            skLineSegment(sketch, "E261.MirrorCS", {"start": v(1.9, -12.07) * mm, "end": v(1.9, -10.8) * mm});
            skLineSegment(sketch, "E262.MirrorCS", {"start": v(-0.63, -9.53) * mm, "end": v(-0.64, -8.26) * mm});
            skLineSegment(sketch, "E263.MirrorCS", {"start": v(14.6, -14.6) * mm, "end": v(14.6, -13.34) * mm});
            skLineSegment(sketch, "E264.MirrorCS", {"start": v(12.07, -12.07) * mm, "end": v(12.07, -10.8) * mm});
            skLineSegment(sketch, "E265.MirrorCS", {"start": v(9.53, -9.53) * mm, "end": v(9.53, -8.26) * mm});
            skLineSegment(sketch, "E266.MirrorCS", {"start": v(6.99, -6.99) * mm, "end": v(6.99, -5.72) * mm});
            skLineSegment(sketch, "E267.MirrorCS", {"start": v(19.69, -9.53) * mm, "end": v(19.69, -8.26) * mm});
            skLineSegment(sketch, "E268.MirrorCS", {"start": v(17.15, -6.99) * mm, "end": v(17.15, -5.72) * mm});
            skLineSegment(sketch, "E269.MirrorCS", {"start": v(17.15, -17.15) * mm, "end": v(17.15, -15.88) * mm});
            skLineSegment(sketch, "E270.MirrorCS", {"start": v(-12.07, -8.26) * mm, "end": v(-10.8, -8.26) * mm});
            skLineSegment(sketch, "E271.MirrorCS", {"start": v(-14.6, -5.72) * mm, "end": v(-13.34, -5.72) * mm});
            skLineSegment(sketch, "E272.MirrorCS", {"start": v(-14.6, -15.88) * mm, "end": v(-13.34, -15.88) * mm});
            skLineSegment(sketch, "E273.MirrorCS", {"start": v(-17.15, -13.34) * mm, "end": v(-15.88, -13.34) * mm});
            skLineSegment(sketch, "E274.MirrorCS", {"start": v(-4.45, -5.72) * mm, "end": v(-3.18, -5.72) * mm});
            skLineSegment(sketch, "E275.MirrorCS", {"start": v(-4.45, -15.88) * mm, "end": v(-3.18, -15.88) * mm});
            skLineSegment(sketch, "E276.MirrorCS", {"start": v(-6.99, -13.34) * mm, "end": v(-5.72, -13.34) * mm});
            skLineSegment(sketch, "E277.MirrorCS", {"start": v(-9.53, -10.8) * mm, "end": v(-8.26, -10.8) * mm});
            skLineSegment(sketch, "E278.MirrorCS", {"start": v(5.72, -15.88) * mm, "end": v(6.99, -15.88) * mm});
            skLineSegment(sketch, "E279.MirrorCS", {"start": v(3.18, -13.34) * mm, "end": v(4.45, -13.34) * mm});
            skLineSegment(sketch, "E280.MirrorCS", {"start": v(0.64, -10.8) * mm, "end": v(1.9, -10.8) * mm});
            skLineSegment(sketch, "E281.MirrorCS", {"start": v(-1.9, -8.26) * mm, "end": v(-0.64, -8.26) * mm});
            skLineSegment(sketch, "E282.MirrorCS", {"start": v(13.34, -13.34) * mm, "end": v(14.6, -13.34) * mm});
            skLineSegment(sketch, "E283.MirrorCS", {"start": v(10.8, -10.8) * mm, "end": v(12.07, -10.8) * mm});
            skLineSegment(sketch, "E284.MirrorCS", {"start": v(8.26, -8.26) * mm, "end": v(9.53, -8.26) * mm});
            skLineSegment(sketch, "E285.MirrorCS", {"start": v(5.72, -5.72) * mm, "end": v(6.99, -5.72) * mm});
            skLineSegment(sketch, "E286.MirrorCS", {"start": v(18.42, -8.26) * mm, "end": v(19.69, -8.26) * mm});
            skLineSegment(sketch, "E287.MirrorCS", {"start": v(15.88, -5.72) * mm, "end": v(17.15, -5.72) * mm});
            skLineSegment(sketch, "E288.MirrorCS", {"start": v(15.88, -15.88) * mm, "end": v(17.15, -15.88) * mm});
            skLineSegment(sketch, "E289.MirrorCS", {"start": v(-12.07, -6.99) * mm, "end": v(-10.8, -6.99) * mm});
            skLineSegment(sketch, "E290.MirrorCS", {"start": v(-14.6, -14.6) * mm, "end": v(-13.34, -14.6) * mm});
            skLineSegment(sketch, "E291.MirrorCS", {"start": v(-12.07, -17.15) * mm, "end": v(-10.8, -17.15) * mm});
            skLineSegment(sketch, "E292.MirrorCS", {"start": v(-17.15, -12.07) * mm, "end": v(-15.88, -12.07) * mm});
            skLineSegment(sketch, "E293.MirrorCS", {"start": v(-4.45, -14.6) * mm, "end": v(-3.18, -14.6) * mm});
            skLineSegment(sketch, "E294.MirrorCS", {"start": v(-1.9, -17.15) * mm, "end": v(-0.64, -17.15) * mm});
            skLineSegment(sketch, "E295.MirrorCS", {"start": v(-6.99, -12.07) * mm, "end": v(-5.72, -12.07) * mm});
            skLineSegment(sketch, "E296.MirrorCS", {"start": v(-9.53, -9.53) * mm, "end": v(-8.26, -9.53) * mm});
            skLineSegment(sketch, "E297.MirrorCS", {"start": v(5.72, -14.6) * mm, "end": v(6.99, -14.6) * mm});
            skLineSegment(sketch, "E298.MirrorCS", {"start": v(3.18, -12.07) * mm, "end": v(4.45, -12.07) * mm});
            skLineSegment(sketch, "E299.MirrorCS", {"start": v(0.64, -9.53) * mm, "end": v(1.9, -9.53) * mm});
            skLineSegment(sketch, "E300.MirrorCS", {"start": v(-1.9, -6.99) * mm, "end": v(-0.64, -6.99) * mm});
            skLineSegment(sketch, "E301.MirrorCS", {"start": v(13.34, -12.07) * mm, "end": v(14.6, -12.07) * mm});
            skLineSegment(sketch, "E302.MirrorCS", {"start": v(10.8, -9.53) * mm, "end": v(12.07, -9.53) * mm});
            skLineSegment(sketch, "E303.MirrorCS", {"start": v(8.26, -6.99) * mm, "end": v(9.53, -6.99) * mm});
            skLineSegment(sketch, "E304.MirrorCS", {"start": v(8.26, -17.15) * mm, "end": v(9.53, -17.15) * mm});
            skLineSegment(sketch, "E305.MirrorCS", {"start": v(18.42, -6.99) * mm, "end": v(19.69, -6.99) * mm});
            skLineSegment(sketch, "E306.MirrorCS", {"start": v(18.42, -17.15) * mm, "end": v(19.69, -17.15) * mm});
            skLineSegment(sketch, "E307.MirrorCS", {"start": v(15.88, -14.6) * mm, "end": v(17.15, -14.6) * mm});
            skLineSegment(sketch, "E308.MirrorCS", {"start": v(-19.69, -9.53) * mm, "end": v(-19.69, -8.26) * mm});
            skLineSegment(sketch, "E309.MirrorCS", {"start": v(-18.42, -9.53) * mm, "end": v(-18.42, -8.26) * mm});
            skLineSegment(sketch, "E310.MirrorCS", {"start": v(-19.69, -8.26) * mm, "end": v(-18.42, -8.26) * mm});
            skLineSegment(sketch, "E311.MirrorCS", {"start": v(-19.69, -17.15) * mm, "end": v(-18.42, -17.15) * mm});
            skLineSegment(sketch, "E312.MirrorCS", {"start": v(-19.69, -15.88) * mm, "end": v(-18.42, -15.88) * mm});
            skLineSegment(sketch, "E313.MirrorCS", {"start": v(-19.69, -17.15) * mm, "end": v(-19.69, -15.88) * mm});
            skLineSegment(sketch, "E314.MirrorCS", {"start": v(-18.42, -17.15) * mm, "end": v(-18.42, -15.88) * mm});
            skLineSegment(sketch, "E315.MirrorCS", {"start": v(-19.69, -14.6) * mm, "end": v(-18.42, -14.6) * mm});
            skLineSegment(sketch, "E316.MirrorCS", {"start": v(-19.69, -14.6) * mm, "end": v(-19.69, -13.34) * mm});
            skLineSegment(sketch, "E317.MirrorCS", {"start": v(-18.42, -14.6) * mm, "end": v(-18.42, -13.34) * mm});
            skLineSegment(sketch, "E318.MirrorCS", {"start": v(-19.69, -13.34) * mm, "end": v(-18.42, -13.34) * mm});
            skLineSegment(sketch, "E319.MirrorCS", {"start": v(-19.69, -12.07) * mm, "end": v(-18.42, -12.07) * mm});
            skLineSegment(sketch, "E320.MirrorCS", {"start": v(-19.69, -12.07) * mm, "end": v(-19.69, -10.8) * mm});
            skLineSegment(sketch, "E321.MirrorCS", {"start": v(-18.42, -12.07) * mm, "end": v(-18.42, -10.8) * mm});
            skLineSegment(sketch, "E322.MirrorCS", {"start": v(-19.69, -9.53) * mm, "end": v(-18.42, -9.53) * mm});
            skLineSegment(sketch, "E323.MirrorCS", {"start": v(-19.69, -10.8) * mm, "end": v(-18.42, -10.8) * mm});
            skSolve(sketch);
        }
        {
            var Q0;
            Q0 = qSketchRegion(id + "F2", true);
            extrude(context, id + "F3", {"entities" : qUnion([Q0]), "operationType" : NewBodyOperationType.REMOVE, "oppositeDirection" : true, "depth" : 6.35 * mm});
        }
    });
